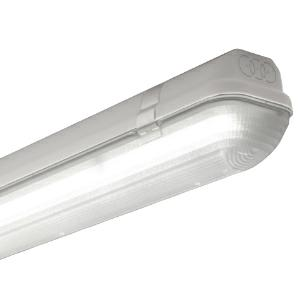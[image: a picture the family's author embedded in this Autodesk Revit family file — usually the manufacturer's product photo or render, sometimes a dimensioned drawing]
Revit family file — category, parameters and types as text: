
# Revit family: 3f_filippi_-_3f_linda_sensor_bluetooth_3f_filippi_-_58786_-_3f_linda_led_1x24w_sensor_dali-ble_l1270
name_source: partatom
category: Lighting Fixtures
units: mm (PartAtom-declared; Revit-internal decimal feet)

## family parameters
Cut with Voids When Loaded = No
Host = Face
Light Source = No
Part Type = Normal
Room Calculation Point = No
Round Connector Dimension = Use Diameter
Shared = No

## types (1)
- 3F Filippi - 3F Linda Sensor Bluetooth (1 x LED, 4065 lm, 29 W, 4000 K)
    Apparent Load = 29 VA
    Approval mark = ENEC
    CIE Flux Codes = 44 77 94 97 100
    Color Rendering = 80
    Color Temperature = 4000 K
    Control Gear = Electronic transformer
    Default Elevation = 1800 mm
    Description = ILLUMINOTECHNICAL
Luminous efficiency 100% (DLOR 97%, ULOR 3%).
Initial luminous flux of the luminaire 4065 lm.
Controlled symmetric distribution.
Installation Interdistance Transv.D = 1.77 x hu - Long.D = 1.17 x hu.
Tabular UGR (CIE 117 - 4H-8H; S=0.25H; 70/50/20): RUG 22 - 22.9.
Beam angle: 109° - 64°.
Luminous efficacy 140 lm/W.
Lifetime (L93/B10): 30000 h. (tq+25°C)
Lifetime (L90/B10): 50000 h. (tq+25°C)
Lifetime (L85/B10): 80000 h. (tq+25°C)
Lifetime (L80/B10): 100000 h. (tq+25°C)
Lifetime (L85/B10): 50000 h. (tq+35°C)
Sudden decreased luminous flux after 50000 hours: 0% (C0).
Photobiological safety in compliance with IEC/TR 62778: RG0 risk exempt, (IEC 62471).
In compliance with IEC/EN 62722-2-1 - IEC/EN 62717 standards.

SOURCE
Linear LED module 24W/840.
Energy efficiency class (UE 2019/2020 - UE 2019/2015): D.
CIE 13.3 Colour rendering index: CRI >80 (R9 <50%).
IES TM-30 Fidelity Index: Rf = 84 Rg = 95.
CCT nominal colour temperature 4000 K.
Colour initial tolerance (MacAdam): SDCM 3.

MECHANICAL
Self-extinguishing V2 polycarbonate housing, injection moulded, RAL 7035 grey.
Ecologic anti-aging injected sealing gasket.
Diffuser in self-extinguishing V2 polycarbonate, photo-engraved interior, UV stabilised, injection moulded with smooth outer surface, tamper-proof opening.
Gear-holder reflector in hot-dip galvanised steel, painted with white polyester base.
Snug fit safety snap-lock clips for diffuser mounting in stainless steel, screwdriver opening.
Fixing brackets in stainless steel.
Possibility for technicians to access the interior of the luminaire.
Luminaire with limited surface temperature. - D - (EN 60598-2-24)
Dimensions: 1270x100 mm, height 100 mm. Weight 2.049 kg.
IP66 protection degree.
Mechanical strength to impacts IK10 (20 joule).
Glow-wire test resistance 850°C.

ELECTRICAL
Halogen Free DALI electronic wiring 230V-50/60Hz, power factor 0.75 at full load, THD <25%, constant output current, SELV, class I, 1 driver, 1 DALI addresse.
High frequency radar motion sensor with Bluetooth interface, integrated in the luminarie.
Power of the luminaire 29 W.
CE - IEC 60598-1 - EN 60598-1.
SAFE FLICKER: PstLM=<1 and SVM=<0.4 (IEC TR 61547-1 and IEC TR 63158), to ensure a more comfortable and safe light.
Ambient temperature from -20°C to +35°C.
Temperature class T6 max 85°C.
Relative humidity UR: <85%.

INSTALLATION
Ceiling / Suspended / Wall.
All accessories dedicated to this product are available on the Catalog and on our website www.3F-Filippi.com.

APPLICATIONS
Suitable product for food production plants (HACCP), IFS (Food Version 6), BRC (GSFS Food Version 7).
Dry, dusty indoor environments, subject to occasional water splashes.
Virtually shatterproof polycarbonate compatibly with the fumes / atmospheres that compromise the elasticity of plastic materials.
Not suitable for installation on surfaces subject to important vibrations, exposed to weather conditions, on ropes or poles.
Suitable for illumination of public car parks and parking grounds referred to DIN 67528:2018-04.

LIGHT MANAGEMENT
Recommended minimum setting: 10%.
The Bluetooth presence sensor integrated in the luminaire allows it to be turned on/off as a result of presence detection and the twilight threshold set.
It also allows adjustment of the luminous flux and creation of a wireless network between DALI-BLE luminaires via the APP Free.
Commissioning of the control system via free APP; the intervention of a specialist technician can be quoted on request.

WARNING
Fixture not suitable for cold stores with an ambient temperature <0°C and/or relative humidity >85%.
Luminaire designed for disposal/recycling at end-of-life.
Replaceable (LED only) light source by a professional. Replaceable control gear by a professional.
    Height = 100 mm  [stored 0.328084 ft]
    Lamp = 1 x LED
    Lamp Light Flux = 4065 lm
    Lamp Power = 29 W
    Lamp count = 1
    Length = 1270 mm
    Lifetime = 50000 h
    Luminous efficacy = 140 lm/W
    Manufacturer = 3F Filippi
    ModVariant = No
    Model = 3F Filippi - 58786 - 3F Linda LED 1x24W Sensor DALI-BLE L1270
    Mounting Place = Ceiling
    Mounting Type = Pendant
    Number of Poles = 1
    OnlyDefault = Yes
    Power Factor = 1
    Product Name = 3F Filippi - 3F Linda Sensor Bluetooth
    Product group = pendant luminaire
    ProductGroupID = 9
    Protection Class = Protection class I
    Protection Degree = IP 66
    RLX_Detail_Level = 1
    RLX_Emergency_Light_Flux = 0 lm
    RLX_Emergency_Type = 0
    RLX_Emergency_Type_DB = No
    RlxData = <blob elided: 72117 chars, md5=579a38cd>
    Socket = socket
    Standby Power = 0 W
    System Light Flux = 4065 lm
    System Power = 29 W
    Type Comments = Product without accessories
    Type Image = 3ffilippi_3f_linda_led.jpg
    URL = http://relux.com
    VarID = ---
    Voltage = 0 V
    Weight = 0.00 kg
    Width = 100 mm  [stored 0.328084 ft]

note: [stored X ft] marks values corroborated as IEEE doubles in the binary element streams (Revit-internal decimal feet)

## geometry (parser evidence)
native form markers: Blend x4, Sweep x9
no freeform markers — native parametric forms only
